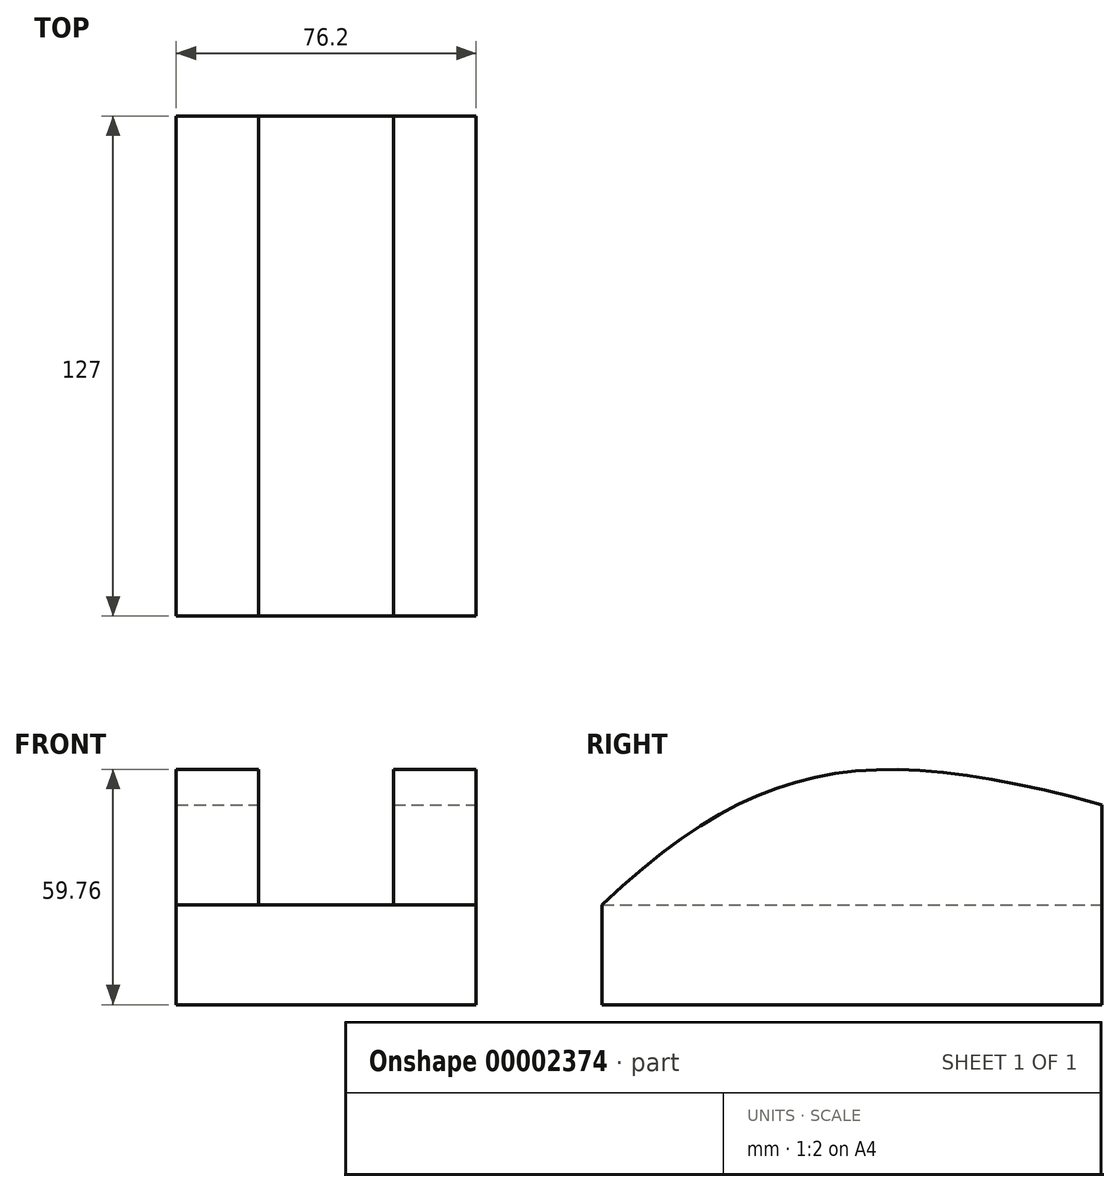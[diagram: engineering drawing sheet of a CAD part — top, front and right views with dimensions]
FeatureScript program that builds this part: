
annotation { "Feature Type Name" : "Feature", "Feature Type Description" : "" }
export const myFeature = defineFeature(function(context is Context, id is Id, definition is map)
    precondition{}
    {
        {
            var Q0;
            Q0=qCreatedBy(makeId("Top.planeOp"),FACE);
            var sketch = newSketch(context, id + "F0", { "sketchPlane" : qUnion([Q0])});
            skLineSegment(sketch, "E0.rect.bottom", {"start": v(38.1, 63.5) * mm, "end": v(-38.1, 63.5) * mm});
            skLineSegment(sketch, "E0.rect.top", {"start": v(38.1, -63.5) * mm, "end": v(-38.1, -63.5) * mm});
            skLineSegment(sketch, "E0.rect.left", {"start": v(38.1, 63.5) * mm, "end": v(38.1, -63.5) * mm});
            skLineSegment(sketch, "E0.rect.right", {"start": v(-38.1, 63.5) * mm, "end": v(-38.1, -63.5) * mm});
            skPoint(sketch, "E0.rect.middle", {"position": v(0, 0) * mm});
            skSolve(sketch);
        }
        {
            var Q0;
            Q0=qCreatedBy(makeId("Right.planeOp"),FACE);
            var sketch = newSketch(context, id + "F1", { "sketchPlane" : qUnion([Q0])});
            skLineSegment(sketch, "E1", {"start": v(-63.5, 25.4) * mm, "end": v(-63.5, 0) * mm, "construction": true});
            skLineSegment(sketch, "E2", {"start": v(63.5, 0) * mm, "end": v(63.5, 50.8) * mm, "construction": true});
            skFitSpline(sketch, "E3", {"points": [v(-79.8, 8.88) * mm, v(73.07, 48.1) * mm], "startDerivative": vector(155.75, 167.1) * mm, "endDerivative": vector(219.22, -63.56) * mm});
            skSolve(sketch);
        }
        {
            var Q0;
            Q0=sQuery(id+"F1.wireOp",EDGE,"E3");
            extrude(context, id + "F2", {"bodyType" : ExtendedToolBodyType.SURFACE, "surfaceEntities" : qUnion([Q0]), "depth" : 170.4 * mm, "symmetric" : true});
        }
        {
            var Q0;
            Q0=makeQuery(id+"F0.imprint","IMPRINT",FACE,{"disambiguationData":[TD([[makeQuery(id+"F0.imprint","IMPRINT",EDGE,{"derivedFrom":sQuery(id+"F0.wireOp",EDGE,"E0.rect.bottom")}),1.0]])]});
            var Q1;
            Q1=makeQuery(id+"F2.opExtrude","SWEPT_FACE",FACE,{"disambiguationData":[OSD([sQuery(id+"F1.wireOp",EDGE,"E3")])]});
            extrude(context, id + "F3", {"entities" : qUnion([Q0]), "endBound" : BoundingType.UP_TO_SURFACE, "endBoundEntityFace" : qUnion([Q1]), "depth" : 25.4 * mm});
        }
        {
            var Q0;
            Q0=qCreatedBy(makeId("Top.planeOp"),FACE);
            cPlane(context, id + "F4", {"entities" : qUnion([Q0]), "cplaneType" : CPlaneType.OFFSET, "offset" : 25.4 * mm, "width" : 152.4 * mm, "height" : 152.4 * mm});
        }
        {
            var Q0;
            Q0=qCreatedBy(id+"F4.planeOp",FACE);
            var sketch = newSketch(context, id + "F5", { "sketchPlane" : qUnion([Q0])});
            skLineSegment(sketch, "E4.bottom", {"start": v(-17.12, -63.5) * mm, "end": v(17.12, -63.5) * mm});
            skLineSegment(sketch, "E4.top", {"start": v(-17.12, 71.04) * mm, "end": v(17.12, 71.04) * mm});
            skLineSegment(sketch, "E4.left", {"start": v(-17.12, -63.5) * mm, "end": v(-17.12, 71.04) * mm});
            skLineSegment(sketch, "E4.right", {"start": v(17.12, -63.5) * mm, "end": v(17.12, 71.04) * mm});
            skSolve(sketch);
        }
        {
            var Q0;
            Q0 = qSketchRegion(id + "F5", true);
            extrude(context, id + "F6", {"entities" : qUnion([Q0]), "operationType" : NewBodyOperationType.REMOVE, "endBound" : BoundingType.THROUGH_ALL, "depth" : 25.4 * mm});
        }
    });
